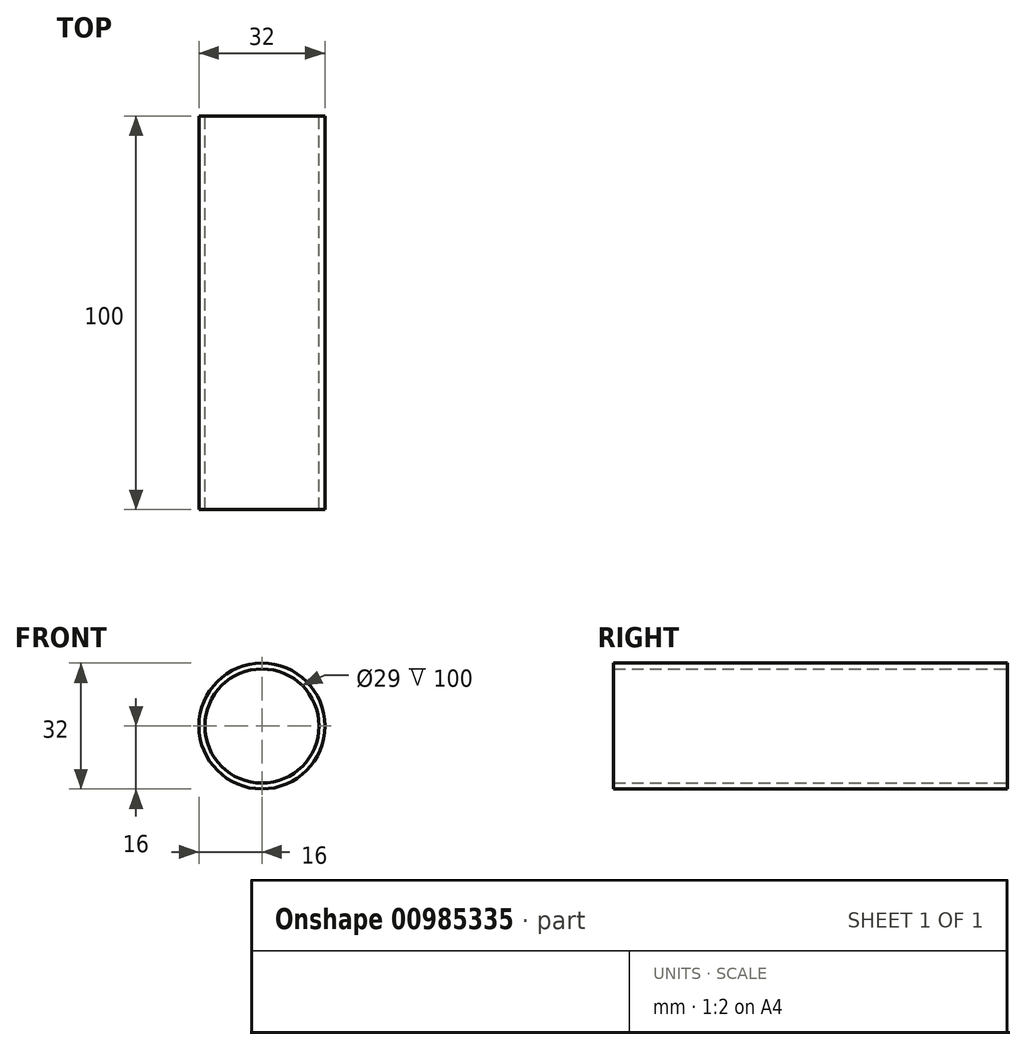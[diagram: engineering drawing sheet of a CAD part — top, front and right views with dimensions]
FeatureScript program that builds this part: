
annotation { "Feature Type Name" : "Feature", "Feature Type Description" : "" }
export const myFeature = defineFeature(function(context is Context, id is Id, definition is map)
    precondition{}
    {
        {
            var Q0;
            Q0=qCreatedBy(makeId("Front.planeOp"),FACE);
            var sketch = newSketch(context, id + "F0", { "sketchPlane" : qUnion([Q0])});
            skCircle(sketch, "E0", {"center": v(0, 0) * mm, "radius": 16 * mm});
            skCircle(sketch, "E1", {"center": v(0, 0) * mm, "radius": 14.5 * mm});
            skSolve(sketch);
        }
        {
            var Q0;
            Q0=makeQuery(id+"F0.imprint","IMPRINT",FACE,{"disambiguationData":[TD([[makeQuery(id+"F0.imprint","IMPRINT",EDGE,{"derivedFrom":sQuery(id+"F0.wireOp",EDGE,"E0")}),1.0]])]});
            extrude(context, id + "F1", {"entities" : qUnion([Q0]), "endBound" : BoundingType.SYMMETRIC, "depth" : 100 * mm});
        }
    });
